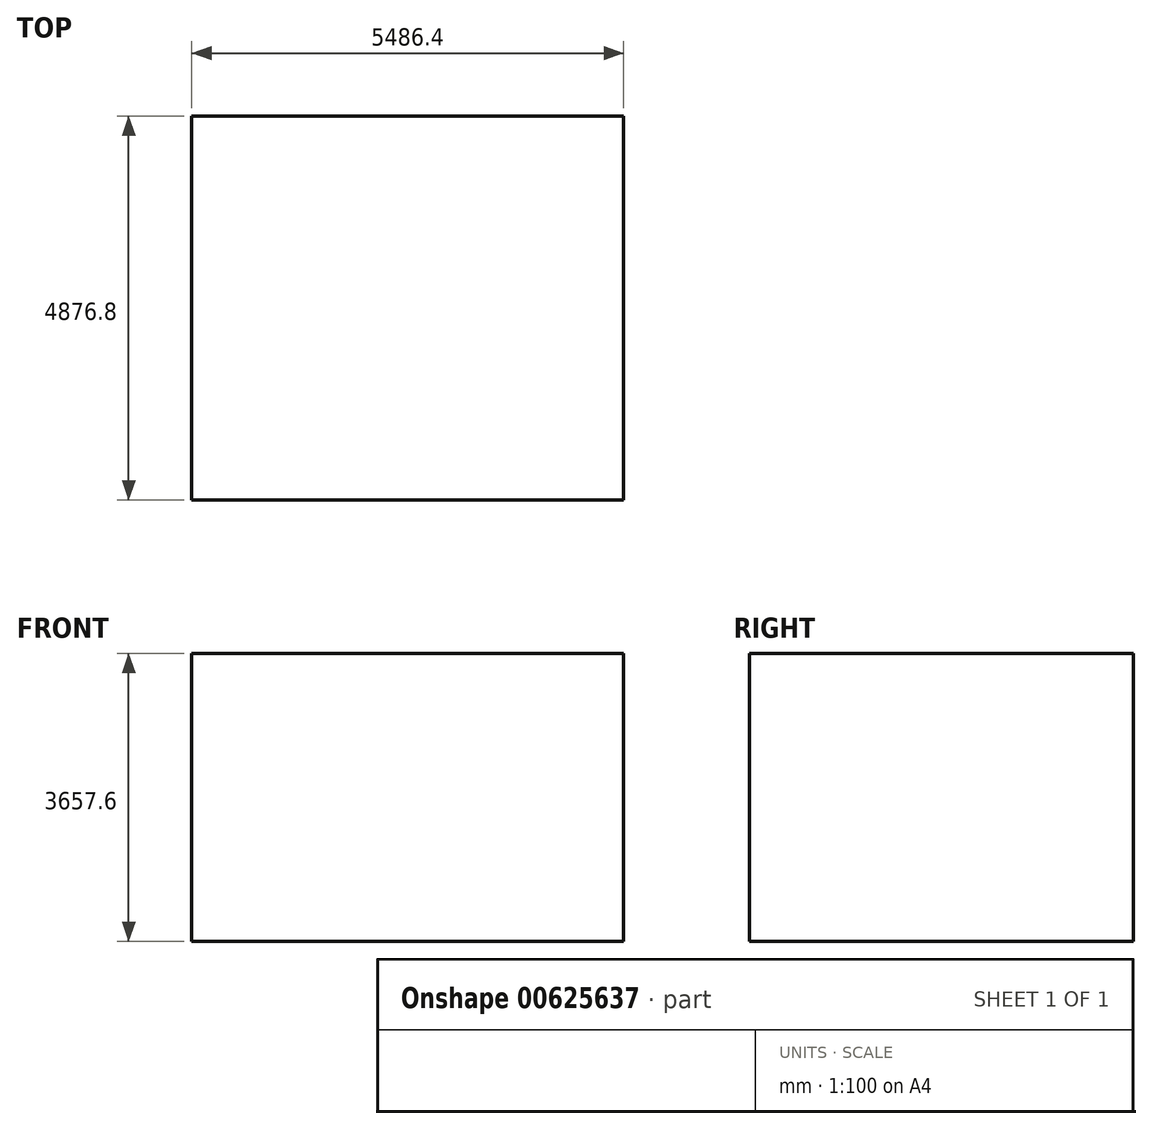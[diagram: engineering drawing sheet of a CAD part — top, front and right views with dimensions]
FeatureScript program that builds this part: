
annotation { "Feature Type Name" : "Feature", "Feature Type Description" : "" }
export const myFeature = defineFeature(function(context is Context, id is Id, definition is map)
    precondition{}
    {
        {
            var Q0;
            Q0=qCreatedBy(makeId("Top.planeOp"),FACE);
            var sketch = newSketch(context, id + "F0", { "sketchPlane" : qUnion([Q0])});
            skLineSegment(sketch, "E0.bottom", {"start": v(2743.2, 2438.4) * mm, "end": v(-2743.2, 2438.4) * mm});
            skLineSegment(sketch, "E0.top", {"start": v(2743.2, -2438.4) * mm, "end": v(-2743.2, -2438.4) * mm});
            skLineSegment(sketch, "E0.right", {"start": v(-2743.2, 2438.4) * mm, "end": v(-2743.2, -2438.4) * mm});
            skPoint(sketch, "E0.middle", {"position": v(0, 0) * mm});
            skSolve(sketch);
        }
        {
            var Q0;
            Q0=sQuery(id+"F0.wireOp",EDGE,"E0.top");
            var Q1;
            Q1=sQuery(id+"F0.wireOp",EDGE,"E0.right");
            var Q2;
            Q2=sQuery(id+"F0.wireOp",EDGE,"E0.bottom");
            var Q3;
            Q3=sQuery(id+"F0.wireOp",EDGE,"E0.left");
            extrude(context, id + "F1", {"bodyType" : ToolBodyType.SURFACE, "surfaceEntities" : qUnion([Q0, Q1, Q2, Q3]), "depth" : 3657.6 * mm, "offsetDistance" : 25.4 * mm});
        }
        {
            var Q0;
            Q0=qCreatedBy(makeId("Front.planeOp"),FACE);
            var sketch = newSketch(context, id + "F2", { "sketchPlane" : qUnion([Q0])});
            skLineSegment(sketch, "E1.0", {"start": v(2743.2, 0) * mm, "end": v(-2743.2, 0) * mm});
            skSolve(sketch);
        }
        {
            var Q0;
            Q0 = qSketchRegion(id + "F2", true);
            var Q1;
            Q1=sQuery(id+"F2.wireOp",EDGE,"E1.0");
            var Q2;
            Q2=makeQuery(id+"F1.opExtrude","SWEPT_FACE",FACE,{"disambiguationData":[OSD([sQuery(id+"F0.wireOp",EDGE,"E0.top")])]});
            var Q3;
            Q3=makeQuery(id+"F1.opExtrude","SWEPT_FACE",FACE,{"disambiguationData":[OSD([sQuery(id+"F0.wireOp",EDGE,"E0.bottom")])]});
            extrude(context, id + "F3", {"entities" : qUnion([Q0]), "bodyType" : ToolBodyType.SURFACE, "surfaceEntities" : qUnion([Q1]), "endBound" : BoundingType.UP_TO_SURFACE, "depth" : 203.2 * mm, "endBoundEntityFace" : qUnion([Q2]), "offsetDistance" : 25.4 * mm, "hasSecondDirection" : true, "secondDirectionBound" : SecondDirectionBoundingType.UP_TO_SURFACE, "secondDirectionOppositeDirection" : true, "secondDirectionDepth" : 25.4 * mm, "secondDirectionBoundEntityFace" : qUnion([Q3])});
        }
    });
